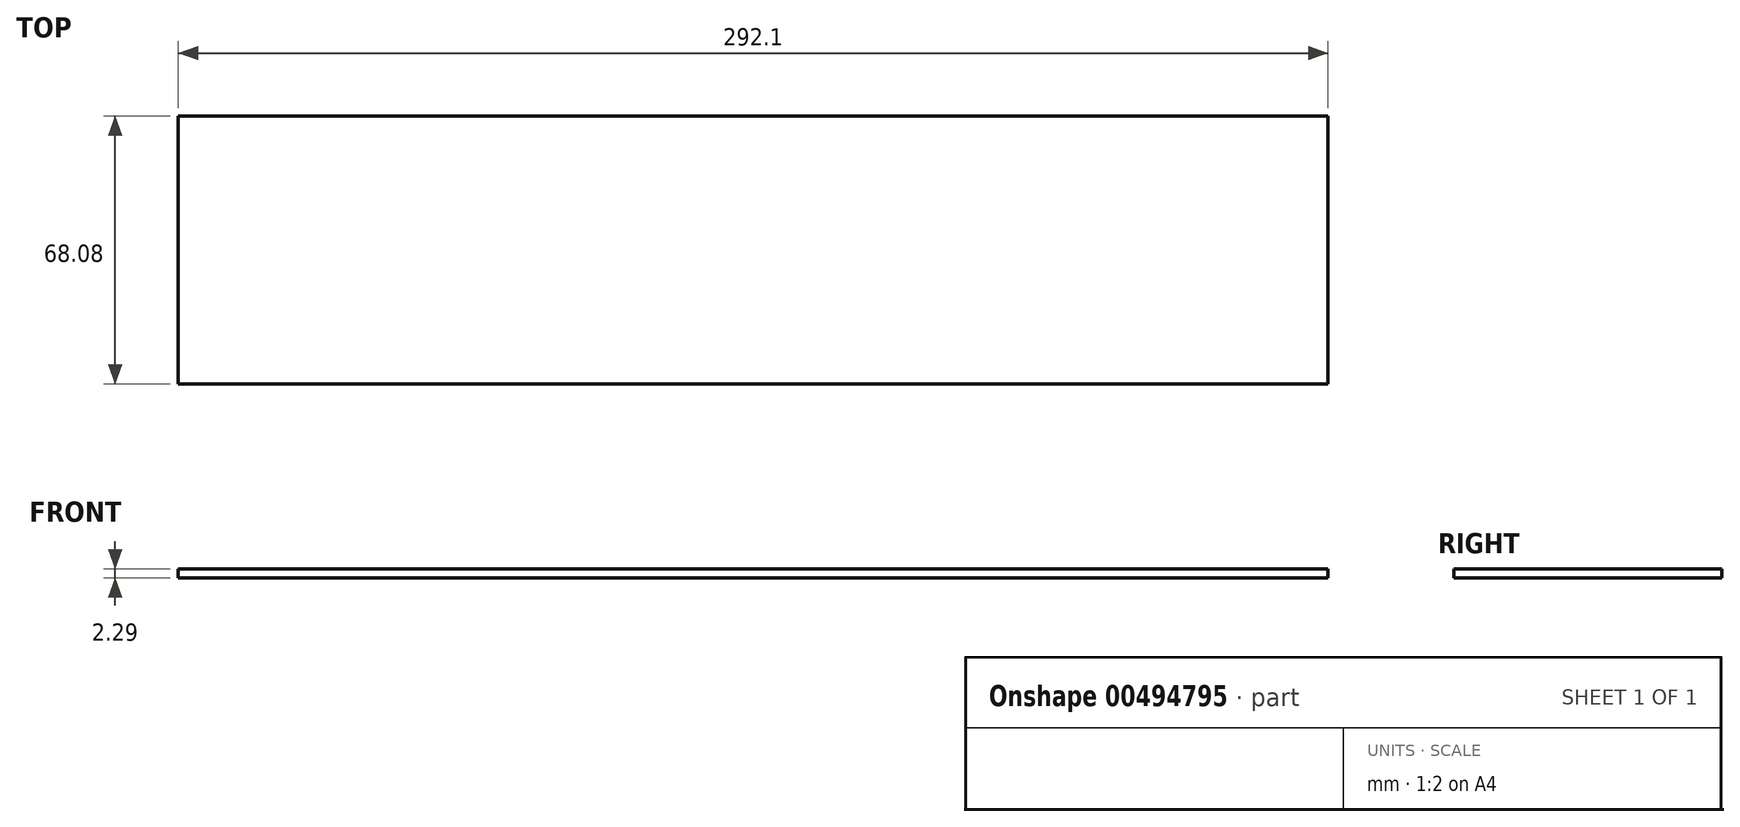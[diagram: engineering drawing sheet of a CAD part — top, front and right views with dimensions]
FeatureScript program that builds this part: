
annotation { "Feature Type Name" : "Feature", "Feature Type Description" : "" }
export const myFeature = defineFeature(function(context is Context, id is Id, definition is map)
    precondition{}
    {
        {
            var Q0;
            Q0=qCreatedBy(makeId("Top.planeOp"),FACE);
            var sketch = newSketch(context, id + "F0", { "sketchPlane" : qUnion([Q0])});
            skLineSegment(sketch, "E0.bottom", {"start": v(146.05, -34.04) * mm, "end": v(-146.05, -34.04) * mm});
            skLineSegment(sketch, "E0.top", {"start": v(146.05, 34.04) * mm, "end": v(-146.05, 34.04) * mm});
            skLineSegment(sketch, "E0.left", {"start": v(146.05, -34.04) * mm, "end": v(146.05, 34.04) * mm});
            skLineSegment(sketch, "E0.right", {"start": v(-146.05, -34.04) * mm, "end": v(-146.05, 34.04) * mm});
            skPoint(sketch, "E0.middle", {"position": v(0, 0) * mm});
            skSolve(sketch);
        }
        {
            var Q0;
            Q0=makeQuery(id+"F0.imprint","IMPRINT",FACE,{"disambiguationData":[TD([[makeQuery(id+"F0.imprint","IMPRINT",EDGE,{"derivedFrom":sQuery(id+"F0.wireOp",EDGE,"E0.bottom")}),-1.0]])]});
            extrude(context, id + "F1", {"entities" : qUnion([Q0]), "depth" : 2.3 * mm});
        }
    });
